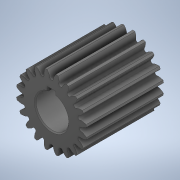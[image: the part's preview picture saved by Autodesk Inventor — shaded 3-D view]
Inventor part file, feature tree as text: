
AUTODESK INVENTOR PART (.ipt)
format: ipt  version: 2020 (Build 240168000, 168)  size: 324,608 bytes
history: native  units: in
note: dims shown in document units (in); Inventor stores cm internally (conversion verified against a paired STEP export)
features: chamfer x1
ambient origin geometry x8: Origin, YZ Plane, XZ Plane, XY Plane, X Axis, Y Axis, Z Axis, Center Point
bodies: Solid1 (feature_tree)
feature tree (1):
  chamfer  "Chamfer1"  [1 undecoded]
note: 1 required parameter value undecoded (feature->parameter linkage not recoverable at this tier; creation-order binding heuristic only, values carry confidence <= 0.55)
